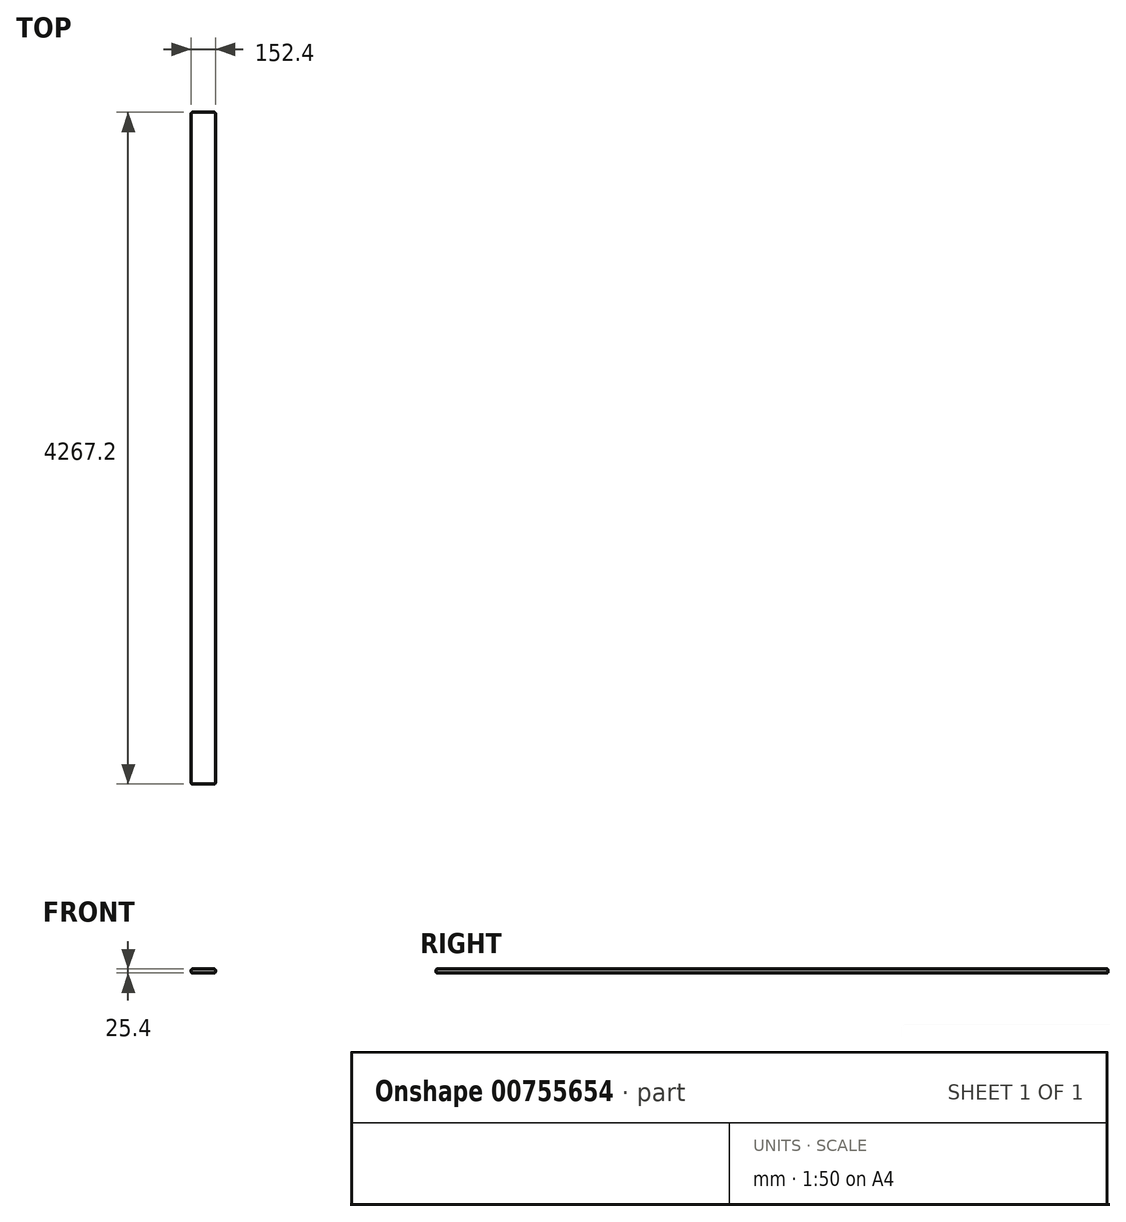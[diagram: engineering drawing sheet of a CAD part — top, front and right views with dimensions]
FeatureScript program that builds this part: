
annotation { "Feature Type Name" : "Feature", "Feature Type Description" : "" }
export const myFeature = defineFeature(function(context is Context, id is Id, definition is map)
    precondition{}
    {
        {
            var Q0;
            Q0=qCreatedBy(makeId("Front.planeOp"),FACE);
            var sketch = newSketch(context, id + "F0", { "sketchPlane" : qUnion([Q0])});
            skLineSegment(sketch, "E0.bottom", {"start": v(69.85, -12.7) * mm, "end": v(-69.85, -12.7) * mm});
            skLineSegment(sketch, "E0.top", {"start": v(69.85, 12.7) * mm, "end": v(-69.85, 12.7) * mm});
            skLineSegment(sketch, "E0.left", {"start": v(76.2, -6.35) * mm, "end": v(76.2, 6.35) * mm});
            skLineSegment(sketch, "E0.right", {"start": v(-76.2, -6.35) * mm, "end": v(-76.2, 6.35) * mm});
            skPoint(sketch, "E0.middle", {"position": v(0, 0) * mm});
            skPoint(sketch, "E1.visualSharp", {"position": v(-76.2, 12.7) * mm});
            skArc(sketch, "E1.filletArc", {"start": v(-69.85, 12.7) * mm, "mid": v(-74.34, 10.84) * mm, "end": v(-76.2, 6.35) * mm});
            skPoint(sketch, "E2.visualSharp", {"position": v(-76.2, -12.7) * mm});
            skArc(sketch, "E2.filletArc", {"start": v(-76.2, -6.35) * mm, "mid": v(-74.34, -10.84) * mm, "end": v(-69.85, -12.7) * mm});
            skPoint(sketch, "E3.visualSharp", {"position": v(76.2, -12.7) * mm});
            skArc(sketch, "E3.filletArc", {"start": v(69.85, -12.7) * mm, "mid": v(74.34, -10.84) * mm, "end": v(76.2, -6.35) * mm});
            skPoint(sketch, "E4.visualSharp", {"position": v(76.2, 12.7) * mm});
            skArc(sketch, "E4.filletArc", {"start": v(76.2, 6.35) * mm, "mid": v(74.34, 10.84) * mm, "end": v(69.85, 12.7) * mm});
            skSolve(sketch);
        }
        {
            var Q0;
            Q0 = qSketchRegion(id + "F0", true);
            extrude(context, id + "F1", {"entities" : qUnion([Q0]), "oppositeDirection" : true, "depth" : 4267.2 * mm, "offsetDistance" : 25.4 * mm});
        }
        {
            var Q0;
            Q0=makeQuery(id+"F1.opExtrude","CAP_EDGE",EDGE,{"disambiguationData":[OSD([sQuery(id+"F0.wireOp",EDGE,"E0.top")])],"isStart":true});
            var Q1;
            Q1=makeQuery(id+"F1.opExtrude","CAP_EDGE",EDGE,{"disambiguationData":[OSD([sQuery(id+"F0.wireOp",EDGE,"E0.bottom")])],"isStart":true});
            fillet(context, id + "F2", {"entities" : qUnion([Q0, Q1]), "radius" : 6.35 * mm, "tangentPropagation" : true, "allowEdgeOverflow" : false});
        }
        {
            var Q0;
            Q0=makeQuery(id+"F1.opExtrude","CAP_EDGE",EDGE,{"disambiguationData":[OSD([sQuery(id+"F0.wireOp",EDGE,"E0.top")])],"isStart":false});
            var Q1;
            Q1=makeQuery(id+"F1.opExtrude","CAP_EDGE",EDGE,{"disambiguationData":[OSD([sQuery(id+"F0.wireOp",EDGE,"E0.left")])],"isStart":false});
            fillet(context, id + "F3", {"entities" : qUnion([Q0, Q1]), "radius" : 6.35 * mm, "tangentPropagation" : true, "allowEdgeOverflow" : false});
        }
    });
